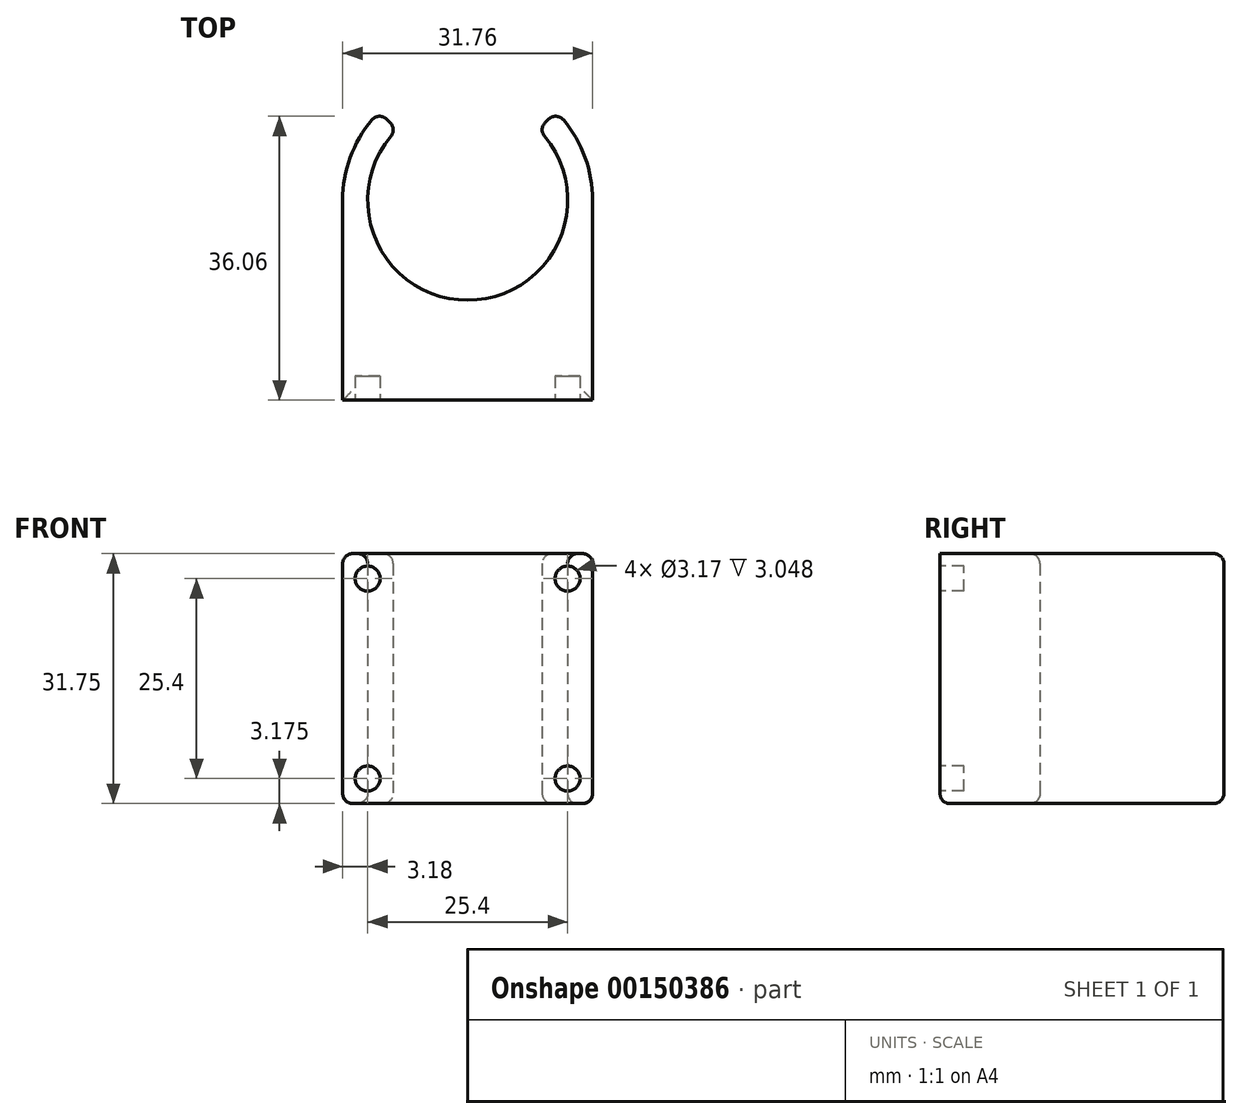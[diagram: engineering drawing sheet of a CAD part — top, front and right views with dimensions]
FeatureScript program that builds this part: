
annotation { "Feature Type Name" : "Feature", "Feature Type Description" : "" }
export const myFeature = defineFeature(function(context is Context, id is Id, definition is map)
    precondition{}
    {
        {
            var Q0;
            Q0=qCreatedBy(makeId("Top.planeOp"),FACE);
            var sketch = newSketch(context, id + "F0", { "sketchPlane" : qUnion([Q0])});
            skArc(sketch, "E0", {"start": v(-8.98, 8.98) * mm, "mid": v(0, -12.7) * mm, "end": v(8.98, 8.98) * mm});
            skArc(sketch, "E1", {"start": v(-11.23, 11.23) * mm, "mid": v(-14.67, 6.08) * mm, "end": v(-15.88, 0) * mm});
            skLineSegment(sketch, "E2", {"start": v(-15.88, 0) * mm, "end": v(-15.88, -25.4) * mm});
            skLineSegment(sketch, "E3", {"start": v(-15.88, -25.4) * mm, "end": v(15.88, -25.4) * mm});
            skLineSegment(sketch, "E4", {"start": v(15.88, -25.4) * mm, "end": v(15.88, 0) * mm});
            skLineSegment(sketch, "E5", {"start": v(-8.98, 8.98) * mm, "end": v(-11.23, 11.23) * mm});
            skLineSegment(sketch, "E6", {"start": v(11.23, 11.23) * mm, "end": v(8.98, 8.98) * mm});
            skArc(sketch, "E7.trimOffspring", {"start": v(15.88, 0) * mm, "mid": v(14.67, 6.08) * mm, "end": v(11.23, 11.23) * mm});
            skSolve(sketch);
        }
        {
            var Q0;
            Q0 = qSketchRegion(id + "F0", true);
            extrude(context, id + "F1", {"entities" : qUnion([Q0]), "depth" : 31.75 * mm});
        }
        {
            var Q0;
            Q0=makeQuery(id+"F1.opExtrude","SWEPT_FACE",FACE,{"disambiguationData":[OSD([sQuery(id+"F0.wireOp",EDGE,"E3")])]});
            var sketch = newSketch(context, id + "F2", { "sketchPlane" : qUnion([Q0])});
            skCircle(sketch, "E8", {"center": v(-12.7, 28.57) * mm, "radius": 1.59 * mm});
            skCircle(sketch, "E9", {"center": v(12.7, 28.57) * mm, "radius": 1.59 * mm});
            skCircle(sketch, "E10", {"center": v(12.7, 3.18) * mm, "radius": 1.59 * mm});
            skCircle(sketch, "E11", {"center": v(-12.7, 3.18) * mm, "radius": 1.59 * mm});
            skLineSegment(sketch, "E12", {"start": v(-12.7, 28.57) * mm, "end": v(-12.7, 3.18) * mm, "construction": true});
            skLineSegment(sketch, "E13", {"start": v(12.7, 3.18) * mm, "end": v(12.7, 28.57) * mm, "construction": true});
            skLineSegment(sketch, "E14", {"start": v(-12.7, 28.57) * mm, "end": v(12.7, 28.57) * mm, "construction": true});
            skLineSegment(sketch, "E15", {"start": v(-12.7, 3.18) * mm, "end": v(12.7, 3.18) * mm, "construction": true});
            skLineSegment(sketch, "E16", {"start": v(0, 0) * mm, "end": v(0, 3.18) * mm, "construction": true});
            skLineSegment(sketch, "E17", {"start": v(-15.88, 15.88) * mm, "end": v(-12.7, 15.88) * mm, "construction": true});
            skSolve(sketch);
        }
        {
            var Q0;
            Q0 = qSketchRegion(id + "F2", true);
            extrude(context, id + "F3", {"entities" : qUnion([Q0]), "operationType" : NewBodyOperationType.REMOVE, "oppositeDirection" : true, "depth" : 3.05 * mm});
        }
        {
            var Q0;
            Q0=makeQuery(id+"F1.opExtrude","CAP_EDGE",EDGE,{"disambiguationData":[OSD([sQuery(id+"F0.wireOp",EDGE,"E2")])],"isStart":false});
            var Q1;
            Q1=makeQuery(id+"F1.opExtrude","CAP_EDGE",EDGE,{"disambiguationData":[OSD([sQuery(id+"F0.wireOp",EDGE,"E0")])],"isStart":false});
            var Q2;
            Q2=makeQuery(id+"F1.opExtrude","CAP_EDGE",EDGE,{"disambiguationData":[OSD([sQuery(id+"F0.wireOp",EDGE,"E4")])],"isStart":false});
            var Q3;
            Q3=makeQuery(id+"F1.opExtrude","CAP_FACE",FACE,{"disambiguationData":[OSD([sQuery(id+"F0.wireOp",EDGE,"E0"),sQuery(id+"F0.wireOp",EDGE,"E1"),sQuery(id+"F0.wireOp",EDGE,"E2"),sQuery(id+"F0.wireOp",EDGE,"E3"),sQuery(id+"F0.wireOp",EDGE,"E4"),sQuery(id+"F0.wireOp",EDGE,"E5"),sQuery(id+"F0.wireOp",EDGE,"E6"),sQuery(id+"F0.wireOp",EDGE,"E7.trimOffspring")])],"isStart":true});
            var Q4;
            Q4=makeQuery(id+"F1.opExtrude","SWEPT_FACE",FACE,{"disambiguationData":[OSD([sQuery(id+"F0.wireOp",EDGE,"E5")])]});
            var Q5;
            Q5=makeQuery(id+"F1.opExtrude","SWEPT_FACE",FACE,{"disambiguationData":[OSD([sQuery(id+"F0.wireOp",EDGE,"E6")])]});
            fillet(context, id + "F4", {"entities" : qUnion([Q0, Q1, Q2, Q3, Q4, Q5]), "radius" : 1.27 * mm, "tangentPropagation" : true, "allowEdgeOverflow" : false});
        }
    });
